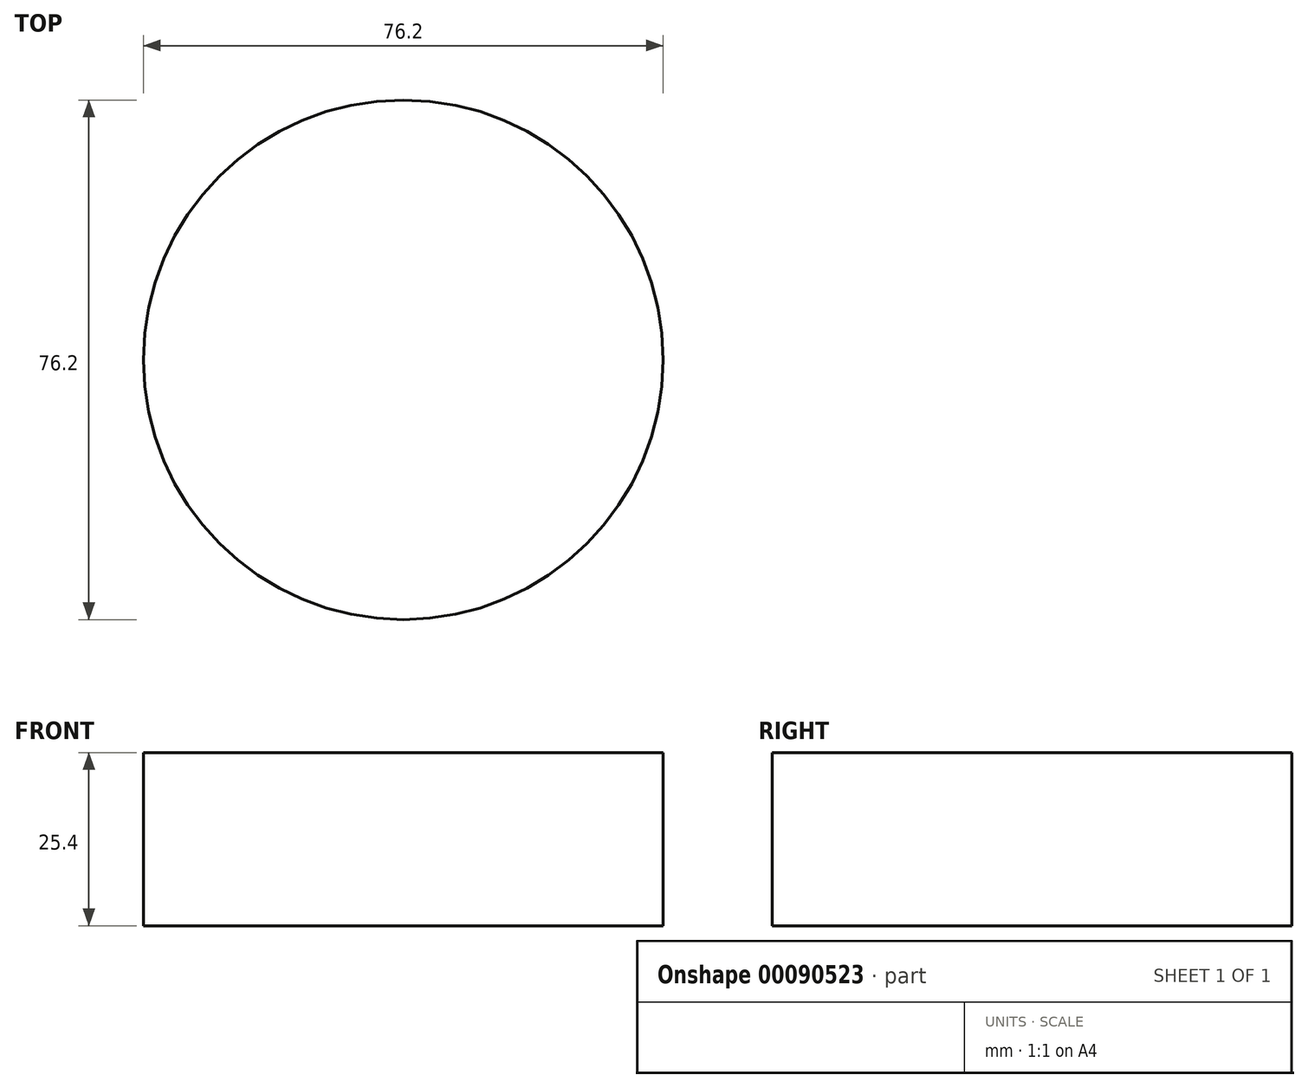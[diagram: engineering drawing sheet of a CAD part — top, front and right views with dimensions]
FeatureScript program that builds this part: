
annotation { "Feature Type Name" : "Feature", "Feature Type Description" : "" }
export const myFeature = defineFeature(function(context is Context, id is Id, definition is map)
    precondition{}
    {
        {
            var Q0;
            Q0=qCreatedBy(makeId("Top.planeOp"),FACE);
            var sketch = newSketch(context, id + "F0", { "sketchPlane" : qUnion([Q0])});
            skPoint(sketch, "E0", {"position": v(-51.74, 53.8) * mm});
            skPoint(sketch, "E1", {"position": v(-51.74, -22.4) * mm});
            skCircle(sketch, "E2", {"center": v(-51.74, 53.8) * mm, "radius": 38.1 * mm});
            skLineSegment(sketch, "E3", {"start": v(-51.74, 3.14) * mm, "end": v(-43.7, 16.55) * mm});
            skLineSegment(sketch, "E4", {"start": v(-51.74, 3.14) * mm, "end": v(-59.79, 16.55) * mm});
            skLineSegment(sketch, "E5.1.0", {"start": v(-21.98, 12.82) * mm, "end": v(-23.35, 28.39) * mm});
            skLineSegment(sketch, "E5.1.1", {"start": v(-21.98, 12.82) * mm, "end": v(-36.36, 18.93) * mm});
            skLineSegment(sketch, "E5.2.0", {"start": v(-3.58, 38.14) * mm, "end": v(-13.84, 49.93) * mm});
            skLineSegment(sketch, "E5.2.1", {"start": v(-3.58, 38.14) * mm, "end": v(-18.81, 34.63) * mm});
            skLineSegment(sketch, "E5.3.0", {"start": v(-3.58, 69.44) * mm, "end": v(-18.81, 72.95) * mm});
            skLineSegment(sketch, "E5.3.1", {"start": v(-3.58, 69.44) * mm, "end": v(-13.84, 57.65) * mm});
            skLineSegment(sketch, "E5.4.0", {"start": v(-21.98, 94.76) * mm, "end": v(-36.36, 88.65) * mm});
            skLineSegment(sketch, "E5.4.1", {"start": v(-21.98, 94.76) * mm, "end": v(-23.35, 79.2) * mm});
            skLineSegment(sketch, "E5.5.0", {"start": v(-51.74, 104.44) * mm, "end": v(-59.79, 91.03) * mm});
            skLineSegment(sketch, "E5.5.1", {"start": v(-51.74, 104.44) * mm, "end": v(-43.7, 91.03) * mm});
            skLineSegment(sketch, "E5.6.0", {"start": v(-81.51, 94.76) * mm, "end": v(-80.14, 79.2) * mm});
            skLineSegment(sketch, "E5.6.1", {"start": v(-81.51, 94.76) * mm, "end": v(-67.13, 88.65) * mm});
            skLineSegment(sketch, "E5.7.0", {"start": v(-99.91, 69.44) * mm, "end": v(-89.65, 57.65) * mm});
            skLineSegment(sketch, "E5.7.1", {"start": v(-99.91, 69.44) * mm, "end": v(-84.68, 72.95) * mm});
            skLineSegment(sketch, "E5.8.0", {"start": v(-99.91, 38.14) * mm, "end": v(-84.68, 34.63) * mm});
            skLineSegment(sketch, "E5.8.1", {"start": v(-99.91, 38.14) * mm, "end": v(-89.65, 49.93) * mm});
            skLineSegment(sketch, "E5.9.0", {"start": v(-81.51, 12.82) * mm, "end": v(-67.13, 18.93) * mm});
            skLineSegment(sketch, "E5.9.1", {"start": v(-81.51, 12.82) * mm, "end": v(-80.14, 28.39) * mm});
            skSolve(sketch);
        }
        {
            var Q0;
            Q0=makeQuery(id+"F0.imprint","IMPRINT",FACE,{"disambiguationData":[TD([[makeQuery(id+"F0.imprint","IMPRINT",EDGE,{"derivedFrom":sQuery(id+"F0.wireOp",EDGE,"YCCCSWK0-zlv3-YyXS-ej1S-xGye6IYwIFmJ")}),1.0]])]});
            var Q1;
            Q1=makeQuery(id+"F0.imprint","IMPRINT",FACE,{"disambiguationData":[TD([[makeQuery(id+"F0.imprint","IMPRINT",EDGE,{"derivedFrom":sQuery(id+"F0.wireOp",EDGE,"E2")}),1.0]])]});
            extrude(context, id + "F1", {"entities" : qUnion([Q0, Q1]), "depth" : 25.4 * mm});
        }
    });
